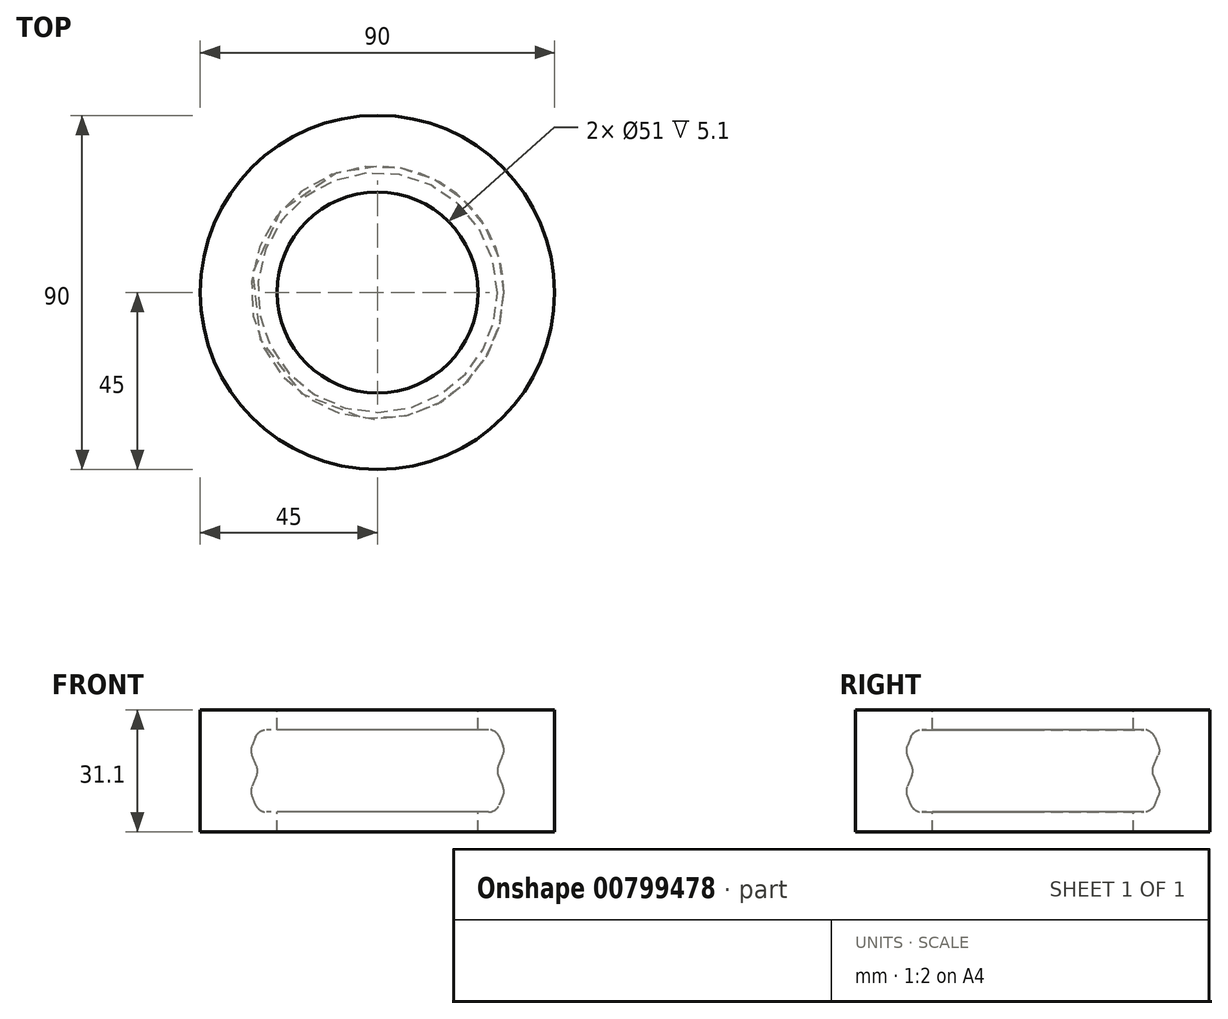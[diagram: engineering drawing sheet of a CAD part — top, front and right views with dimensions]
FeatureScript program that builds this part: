
annotation { "Feature Type Name" : "Feature", "Feature Type Description" : "" }
export const myFeature = defineFeature(function(context is Context, id is Id, definition is map)
    precondition{}
    {
        {
            var Q0;
            Q0=qCreatedBy(makeId("Front.planeOp"),FACE);
            var sketch = newSketch(context, id + "F0", { "sketchPlane" : qUnion([Q0])});
            skLineSegment(sketch, "E0", {"start": v(0, 22.97) * mm, "end": v(45, 22.97) * mm});
            skLineSegment(sketch, "E1", {"start": v(45, 22.97) * mm, "end": v(45, -8.13) * mm});
            skLineSegment(sketch, "E2", {"start": v(45, -8.13) * mm, "end": v(0, -8.13) * mm});
            skLineSegment(sketch, "E3", {"start": v(25.5, -8.13) * mm, "end": v(25.5, -3.03) * mm});
            skPoint(sketch, "E3.startSnap0", {"position": v(25.5, 21.16) * mm});
            skLineSegment(sketch, "E4", {"start": v(25.5, -3.03) * mm, "end": v(0, -3.03) * mm});
            skLineSegment(sketch, "E5", {"start": v(45, 7.42) * mm, "end": v(-35.16, 7.42) * mm, "construction": true});
            skPoint(sketch, "E6", {"position": v(29.96, 7.42) * mm});
            skLineSegment(sketch, "E7", {"start": v(32.13, 2.2) * mm, "end": v(-26.49, 2.2) * mm, "construction": true});
            skLineSegment(sketch, "E8.MirrorCS", {"start": v(32.13, 12.65) * mm, "end": v(-26.49, 12.65) * mm, "construction": true});
            skLineSegment(sketch, "E9", {"start": v(25.5, -3.03) * mm, "end": v(27.96, -3.03) * mm});
            skPoint(sketch, "E10.orphan", {"position": v(25.5, 18.66) * mm});
            skLineSegment(sketch, "E11.MirrorCS", {"start": v(25.5, 17.87) * mm, "end": v(0, 17.87) * mm});
            skLineSegment(sketch, "E12.MirrorCS", {"start": v(25.5, 22.97) * mm, "end": v(25.5, 17.87) * mm});
            skPoint(sketch, "E13.visualSharp", {"position": v(29.96, 17.87) * mm});
            skPoint(sketch, "E14.visualSharp", {"position": v(32.13, 12.65) * mm});
            skPoint(sketch, "E15.visualSharp", {"position": v(32.13, 2.2) * mm});
            skPoint(sketch, "E16.visualSharp", {"position": v(29.96, -3.03) * mm});
            skLineSegment(sketch, "E17", {"start": v(0, 22.97) * mm, "end": v(0, -8.13) * mm});
            skLineSegment(sketch, "E18", {"start": v(32.13, 11.25) * mm, "end": v(32.13, 14.93) * mm, "construction": true});
            skArc(sketch, "E19.filletArc", {"start": v(31.9, 11.5) * mm, "mid": v(32.13, 12.65) * mm, "end": v(31.9, 13.8) * mm});
            skLineSegment(sketch, "E20", {"start": v(31.9, 13.8) * mm, "end": v(30.98, 16.02) * mm});
            skLineSegment(sketch, "E21", {"start": v(25.5, 17.87) * mm, "end": v(28.2, 17.87) * mm});
            skArc(sketch, "E22.filletArc", {"start": v(30.98, 16.02) * mm, "mid": v(29.87, 17.37) * mm, "end": v(28.2, 17.87) * mm});
            skLineSegment(sketch, "E23", {"start": v(31.9, 11.5) * mm, "end": v(30.69, 8.57) * mm});
            skPoint(sketch, "E24.newPointA", {"position": v(28.2, 2.58) * mm});
            skPoint(sketch, "E24.newPointB", {"position": v(30.21, 7.42) * mm});
            skArc(sketch, "E24.filletArc", {"start": v(30.69, 8.57) * mm, "mid": v(30.46, 7.42) * mm, "end": v(30.69, 6.27) * mm});
            skLineSegment(sketch, "E25", {"start": v(30.46, 10.27) * mm, "end": v(30.46, 4.29) * mm, "construction": true});
            skArc(sketch, "E26.MirrorCS", {"start": v(30.69, 6.27) * mm, "mid": v(30.46, 7.42) * mm, "end": v(30.69, 8.57) * mm});
            skLineSegment(sketch, "E27.MirrorCS", {"start": v(31.9, 3.35) * mm, "end": v(30.69, 6.27) * mm});
            skArc(sketch, "E28.MirrorCS", {"start": v(31.9, 3.35) * mm, "mid": v(32.13, 2.2) * mm, "end": v(31.9, 1.05) * mm});
            skArc(sketch, "E29.MirrorCS", {"start": v(30.98, -1.18) * mm, "mid": v(29.87, -2.52) * mm, "end": v(28.2, -3.03) * mm});
            skLineSegment(sketch, "E30.MirrorCS", {"start": v(31.9, 1.05) * mm, "end": v(30.98, -1.18) * mm});
            skLineSegment(sketch, "E31", {"start": v(27.96, -3.03) * mm, "end": v(28.2, -3.03) * mm});
            skSolve(sketch);
        }
        {
            var Q0;
            {var subQ1=sQuery(id+"F0.wireOp",EDGE,"E1");Q0=makeQuery(id+"F0.imprint","IMPRINT",FACE,{"disambiguationData":[TD([[makeQuery(id+"F0.imprint","IMPRINT",EDGE,{"derivedFrom":subQ1}),-1.0]])]});}
            var Q1;
            Q1=sQuery(id+"F0.wireOp",EDGE,"E17");
            revolve(context, id + "F1", {"surfaceOperationType" : NewSurfaceOperationType.NEW, "entities" : qUnion([Q0]), "axis" : qUnion([Q1]), "revolveType" : RevolveType.FULL});
        }
    });
